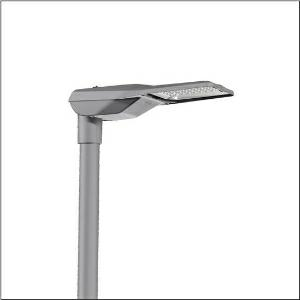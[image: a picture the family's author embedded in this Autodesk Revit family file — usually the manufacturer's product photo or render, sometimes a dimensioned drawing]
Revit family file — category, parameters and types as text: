
# Revit family: streetlight_sl_21_mini___pl52_5xe2h43s08hb_f567
name_source: partatom
category: Lighting Fixtures
units: mm (PartAtom-declared; Revit-internal decimal feet)

## family parameters
Cut with Voids When Loaded = No
Host = Face
Light Source = No
Part Type = Normal
Room Calculation Point = No
Round Connector Dimension = Use Diameter
Shared = No

## types (1)
- --- (1 x LED, 9260 lm, 66 W, 4000K)
    Apparent Load = 66 VA
    CIE Flux Codes = 27 59 98 100 100
    Color Rendering = 70
    Color Temperature = 4000K
    Default Elevation = 1800 mm
    Description = Streetlight SL 21 mini, mast luminaire, primary light control with lens, of PMMA, primary optical cover: cover, of toughened safety glass, transparent, light distribution: PL52, light emission: direct distribution, primary light characteristic: asymmetric, installation type: side-entry, post-top, LED, High Power LED, rated luminous flux: 9.260lm, luminous efficacy: 140lm/W, light colour: 740, colour temperature: 4000K, control gear: D4i, control: overheat protection, constant luminous flux control, time-dependent luminous flux control, flexible luminous flux parameterisation, pre-setting: logarithmic dimming characteristic, mains connection: 220..240V, AC, 50/60Hz, start of lifetime: 66W, end of service life: 69W, reduction: 30W, luminaire housing, of diecast aluminium, powder-coated, SITECO metallic grey (DB 702S), corrosivity category C5 high according to DIN EN ISO 12944, please order mast flange separately, inclination adjustable: 0°, 5°, 10°, 15°, sealing non-destructively replaceable, multi-level sealing system, length: 628mm, width: 235mm, height: 110mm, mast flange for spigot size: 42mm (side-entry): 5XC10008XM4, 60/48mm (side-entry/post-top): 5XC10108XM2, 76/60mm (side-entry/post-top): 5XC10108XM1, mounting height: 4..8m, Smart Interface above, protection rating (complete): IP66, insulation class (complete): insulation class II (safety insulation), certification: CE, ENEC, ENEC+, VDE, impact resistance: IK10, permissible operating ambient temperature for outdoor applications: -40..+50°C, standard-compliant lighting for roads and squares, packaging unit: 1 piece

Light Distribution: PL52
    Height = 110 mm
    Lamp = 1 x LED
    Lamp Light Flux = 9260 lm
    Lamp Power = 66 W
    Lamp count = 1
    Length = 625 mm
    Luminous efficacy = 140 lm/W
    Manufacturer = Siteco
    ModVariant = No
    Model = 5XE2H43S08HB
    Number of Poles = 1
    OnlyDefault = Yes
    Power Factor = 1
    Product Name = Streetlight SL 21 mini | PL52
    Product group = mast luminaire | pylon top
    ProductGroupID = 6100
    Protection Class = Protection class II
    Protection Degree = IP 66
    RLX_Detail_Level = 1
    RLX_Emergency_Light_Flux = 0 lm
    RLX_Emergency_Type = 0
    RLX_Emergency_Type_DB = No
    RlxData = <blob elided: 35765 chars, md5=0860e3ce>
    Socket = socket
    Standby Power = 0 W
    System Light Flux = 9260 lm
    System Power = 66 W
    Type Comments = factory setting: luminous flux: 100 % | dim-lin: 254 | 670 mA
    Type Image = l_1003515.jpg
    URL = http://relux.com
    VarID = @adj_187559
    Voltage = 0 V
    Weight = 0.00 kg
    Width = 234 mm

## geometry (parser evidence)
native form markers: Blend x4, Sweep x10
no freeform markers — native parametric forms only
